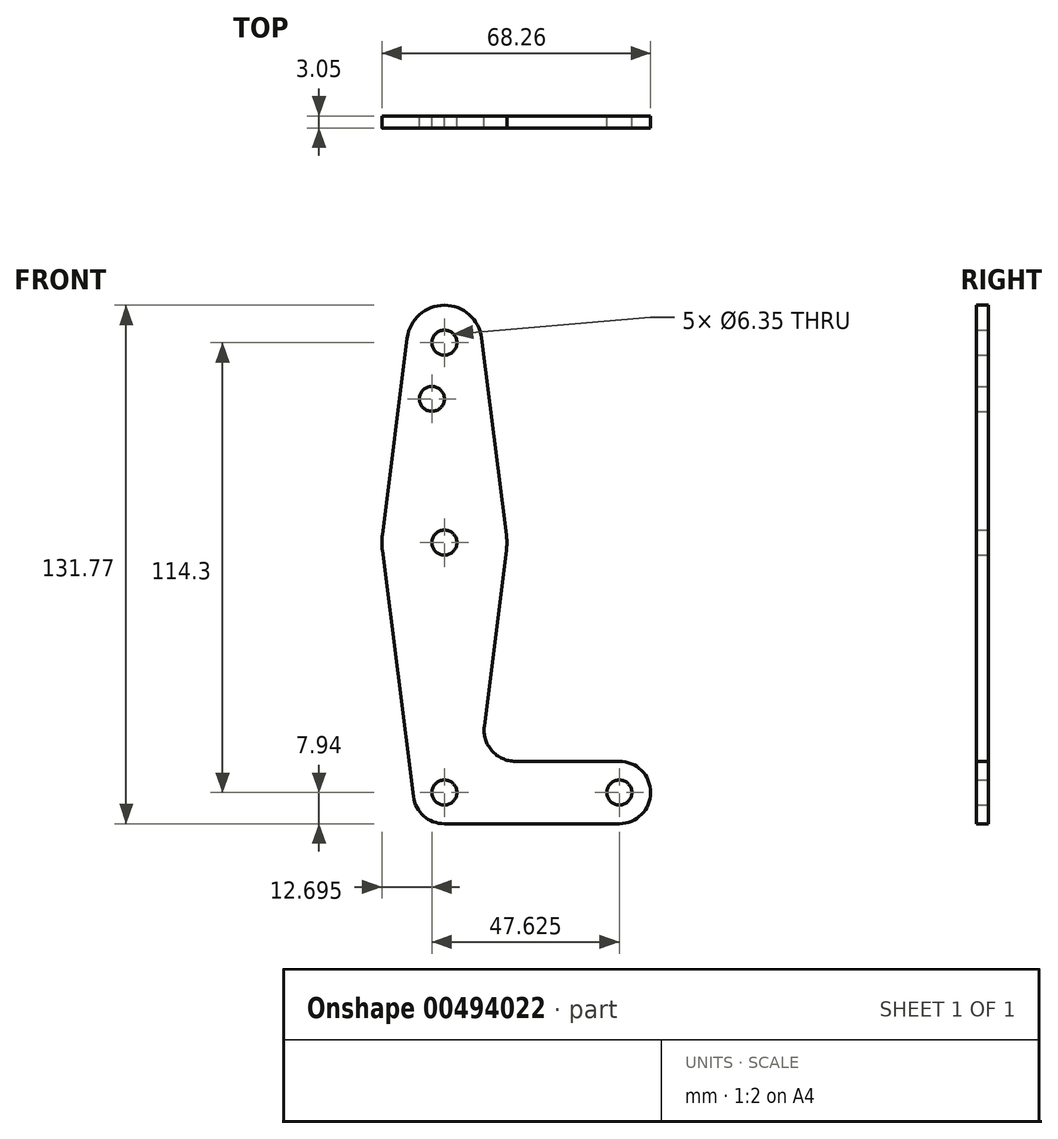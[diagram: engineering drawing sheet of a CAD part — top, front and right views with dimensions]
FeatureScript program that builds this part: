
annotation { "Feature Type Name" : "Feature", "Feature Type Description" : "" }
export const myFeature = defineFeature(function(context is Context, id is Id, definition is map)
    precondition{}
    {
        {
            var Q0;
            Q0=qCreatedBy(makeId("Front.planeOp"),FACE);
            var sketch = newSketch(context, id + "F0", { "sketchPlane" : qUnion([Q0])});
            skLineSegment(sketch, "E0", {"start": v(0, 0) * mm, "end": v(0, 114.3) * mm, "construction": true});
            skLineSegment(sketch, "E1", {"start": v(0, 0) * mm, "end": v(44.45, 0) * mm, "construction": true});
            skCircle(sketch, "E2", {"center": v(0, 114.3) * mm, "radius": 9.53 * mm});
            skCircle(sketch, "E3", {"center": v(0, 63.5) * mm, "radius": 15.88 * mm});
            skCircle(sketch, "E4", {"center": v(0, 0) * mm, "radius": 7.94 * mm});
            skCircle(sketch, "E5", {"center": v(44.45, 0) * mm, "radius": 7.94 * mm});
            skLineSegment(sketch, "E6", {"start": v(-9.45, 115.5) * mm, "end": v(-15.75, 65.48) * mm});
            skLineSegment(sketch, "E7", {"start": v(9.45, 115.5) * mm, "end": v(15.75, 65.48) * mm});
            skLineSegment(sketch, "E8", {"start": v(15.75, 61.52) * mm, "end": v(10.13, 16.88) * mm});
            skLineSegment(sketch, "E9", {"start": v(-15.75, 61.52) * mm, "end": v(-7.88, -1) * mm});
            skLineSegment(sketch, "E10", {"start": v(18.01, 7.94) * mm, "end": v(44.45, 7.94) * mm});
            skLineSegment(sketch, "E11", {"start": v(44.45, -7.94) * mm, "end": v(0, -7.94) * mm});
            skCircle(sketch, "E12", {"center": v(0, 114.3) * mm, "radius": 3.18 * mm});
            skCircle(sketch, "E13", {"center": v(0, 63.5) * mm, "radius": 3.18 * mm});
            skCircle(sketch, "E14", {"center": v(0, 0) * mm, "radius": 3.18 * mm});
            skCircle(sketch, "E15", {"center": v(44.45, 0) * mm, "radius": 3.18 * mm});
            skCircle(sketch, "E16", {"center": v(-3.18, 100.03) * mm, "radius": 3.18 * mm});
            skArc(sketch, "E17.filletArc", {"start": v(10.13, 16.88) * mm, "mid": v(12.05, 10.63) * mm, "end": v(18.01, 7.94) * mm});
            skSolve(sketch);
        }
        {
            var Q0;
            Q0 = qSketchRegion(id + "F0", true);
            extrude(context, id + "F1", {"entities" : qUnion([Q0]), "depth" : 3.05 * mm});
        }
    });
